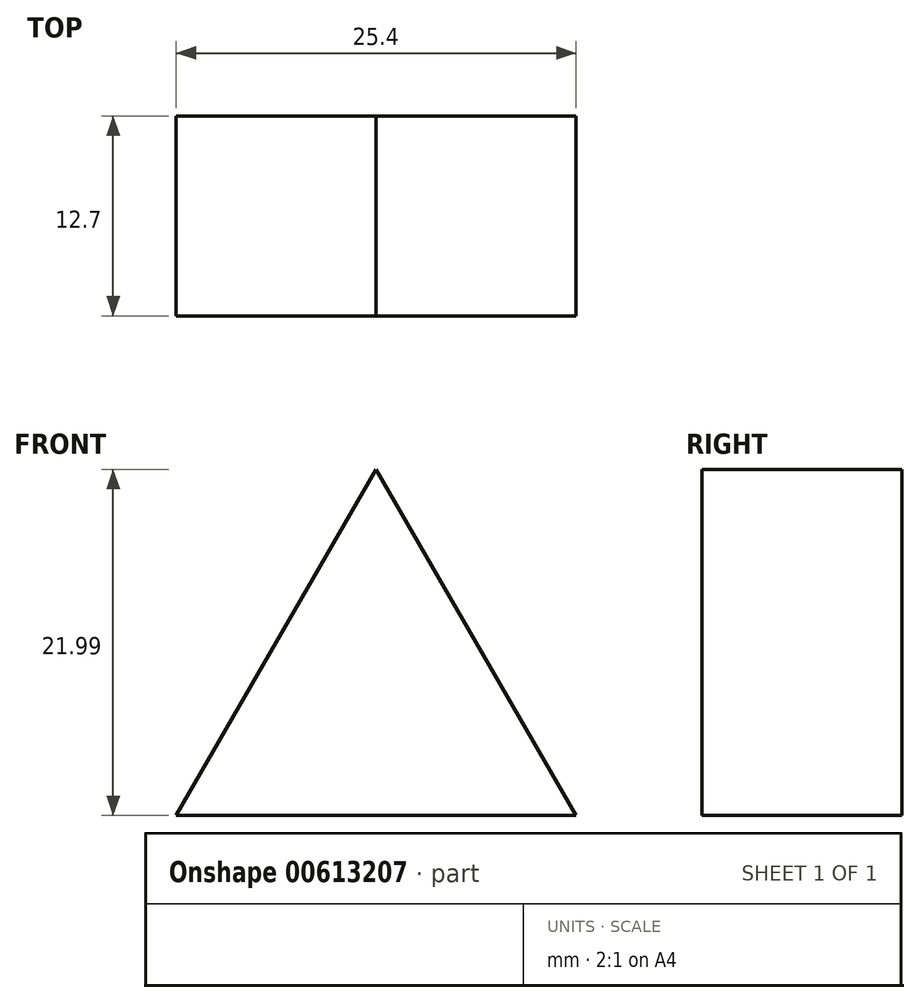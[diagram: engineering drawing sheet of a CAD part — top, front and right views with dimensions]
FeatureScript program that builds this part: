
annotation { "Feature Type Name" : "Feature", "Feature Type Description" : "" }
export const myFeature = defineFeature(function(context is Context, id is Id, definition is map)
    precondition{}
    {
        {
            var Q0;
            Q0=qCreatedBy(makeId("Front.planeOp"),FACE);
            var sketch = newSketch(context, id + "F0", { "sketchPlane" : qUnion([Q0])});
            skLineSegment(sketch, "E0", {"start": v(-55.83, 18.73) * mm, "end": v(-43.13, 40.72) * mm});
            skLineSegment(sketch, "E1", {"start": v(-43.13, 40.72) * mm, "end": v(-30.43, 18.73) * mm});
            skLineSegment(sketch, "E2", {"start": v(-30.43, 18.73) * mm, "end": v(-55.83, 18.73) * mm});
            skSolve(sketch);
        }
        {
            var Q0;
            Q0 = qSketchRegion(id + "F0", true);
            extrude(context, id + "F1", {"entities" : qUnion([Q0]), "depth" : 12.7 * mm, "offsetDistance" : 25.4 * mm});
        }
    });
